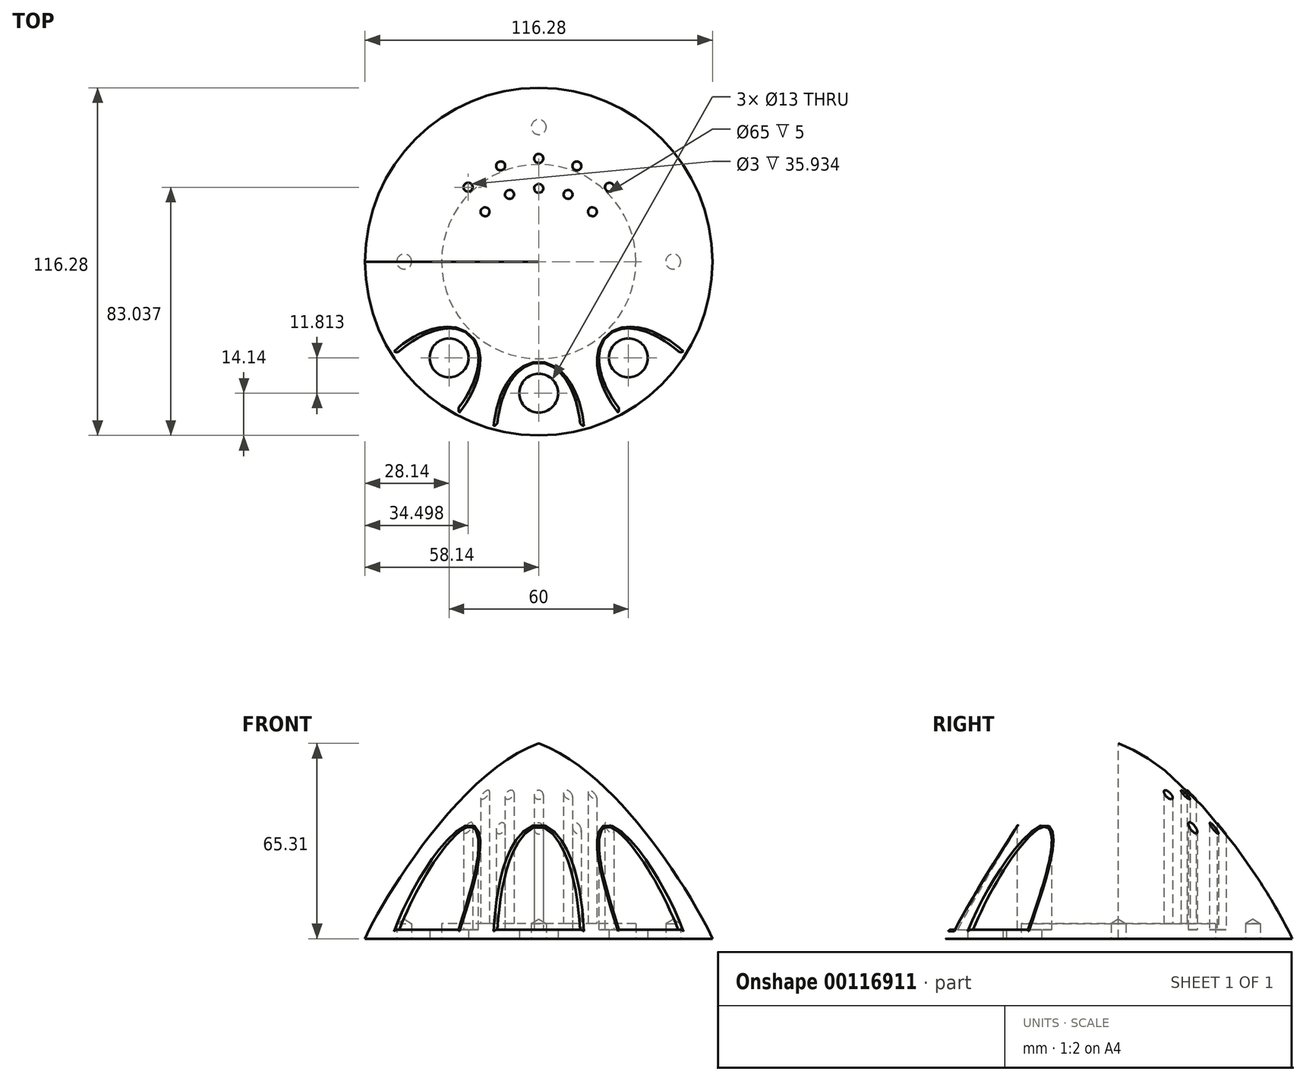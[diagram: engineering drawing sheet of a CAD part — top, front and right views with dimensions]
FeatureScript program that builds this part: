
annotation { "Feature Type Name" : "Feature", "Feature Type Description" : "" }
export const myFeature = defineFeature(function(context is Context, id is Id, definition is map)
    precondition{}
    {
        {
            var Q0;
            Q0=qCreatedBy(makeId("Top.planeOp"),FACE);
            var sketch = newSketch(context, id + "F0", { "sketchPlane" : qUnion([Q0])});
            skCircle(sketch, "E0", {"center": v(0, 0) * mm, "radius": 55 * mm});
            skCircle(sketch, "E1", {"center": v(0, 0) * mm, "radius": 32.5 * mm});
            skCircle(sketch, "E2", {"center": v(0, -44) * mm, "radius": 6.5 * mm});
            skCircle(sketch, "E3", {"center": v(-30, -32.19) * mm, "radius": 6.5 * mm});
            skCircle(sketch, "E4", {"center": v(30, -32.19) * mm, "radius": 6.5 * mm});
            skPoint(sketch, "E5", {"position": v(-45, 0) * mm});
            skPoint(sketch, "E6", {"position": v(0, 45) * mm});
            skPoint(sketch, "E7", {"position": v(45, 0) * mm});
            skSolve(sketch);
        }
        {
            var Q0;
            Q0=qCreatedBy(makeId("Top.planeOp"),FACE);
            var sketch = newSketch(context, id + "F1", { "sketchPlane" : qUnion([Q0])});
            skCircle(sketch, "E8", {"center": v(0, 0) * mm, "radius": 58.13 * mm});
            skPoint(sketch, "E9", {"position": v(-58.13, 0) * mm});
            skSolve(sketch);
        }
        {
            var Q0;
            Q0=qCreatedBy(makeId("Front.planeOp"),FACE);
            var sketch = newSketch(context, id + "F2", { "sketchPlane" : qUnion([Q0])});
            skLineSegment(sketch, "E10", {"start": v(0, 0) * mm, "end": v(-58.13, 0) * mm});
            skLineSegment(sketch, "E11", {"start": v(0, 0) * mm, "end": v(0, 65.3) * mm});
            skFitSpline(sketch, "E12", {"points": [v(-58.13, 0) * mm, v(0, 65.3) * mm], "startDerivative": vector(13.44, 31.02) * mm, "endDerivative": vector(81.7, 28.64) * mm});
            skSolve(sketch);
        }
        {
            var Q0;
            Q0=qCreatedBy(makeId("Top.planeOp"),FACE);
            cPlane(context, id + "F3", {"entities" : qUnion([Q0]), "cplaneType" : CPlaneType.OFFSET, "offset" : 3 * mm, "width" : 150 * mm, "height" : 150 * mm});
        }
        {
            var Q0;
            Q0=makeQuery(id+"F2.imprint","IMPRINT",FACE,{"disambiguationData":[TD([[makeQuery(id+"F2.imprint","IMPRINT",EDGE,{"derivedFrom":sQuery(id+"F2.wireOp",EDGE,"E10")}),-1.0]])]});
            var Q1;
            Q1=sQuery(id+"F2.wireOp",EDGE,"E11");
            revolve(context, id + "F4", {"entities" : qUnion([Q0]), "axis" : qUnion([Q1]), "revolveType" : RevolveType.FULL});
        }
        {
            var Q0;
            Q0=qCreatedBy(id+"F3.planeOp",FACE);
            var sketch = newSketch(context, id + "F5", { "sketchPlane" : qUnion([Q0])});
            skPoint(sketch, "E13", {"position": v(0, -58.13) * mm});
            skPoint(sketch, "E14", {"position": v(0, -33.5) * mm});
            skPoint(sketch, "E15", {"position": v(14, -56.42) * mm});
            skEllipse(sketch, "E16", {"center": v(0, -58.13) * mm, "majorRadius": 24.38 * mm, "minorRadius": 14.03 * mm, "majorAxis": v(0, 1)});
            skLineSegment(sketch, "E17", {"start": v(0, 0) * mm, "end": v(39.64, -42.53) * mm});
            skLineSegment(sketch, "E18", {"start": v(39.64, -42.53) * mm, "end": v(48.65, -31.82) * mm});
            skPoint(sketch, "E19", {"position": v(22.84, -24.5) * mm});
            skEllipse(sketch, "E20", {"center": v(39.64, -42.53) * mm, "majorRadius": 24.39 * mm, "minorRadius": 13.93 * mm, "majorAxis": v(-0.68, 0.73)});
            skLineSegment(sketch, "E21", {"start": v(0, 0) * mm, "end": v(-39.64, -42.53) * mm});
            skLineSegment(sketch, "E22", {"start": v(-39.64, -42.53) * mm, "end": v(-28.32, -50.77) * mm});
            skPoint(sketch, "E23", {"position": v(-22.84, -24.5) * mm});
            skEllipse(sketch, "E24", {"center": v(-39.64, -42.53) * mm, "majorRadius": 24.39 * mm, "minorRadius": 13.93 * mm, "majorAxis": v(0.68, 0.73)});
            skSolve(sketch);
        }
        {
            var Q0;
            Q0=qSketchRegion(id+"F5",true);
            extrude(context, id + "F6", {"entities" : qUnion([Q0]), "operationType" : NewBodyOperationType.REMOVE, "endBound" : BoundingType.THROUGH_ALL, "depth" : 25 * mm});
        }
        {
            var Q0;
            Q0=makeQuery(id+"F6.boolean.opBoolean","INTERSECT",EDGE,{"derivedFrom":[makeQuery(id+"F4.opRevolve","SWEPT_FACE",FACE,{"disambiguationData":[OSD([sQuery(id+"F2.wireOp",EDGE,"E12")])]}),makeQuery(id+"F6.opExtrude","SWEPT_FACE",FACE,{"disambiguationData":[OSD([sQuery(id+"F5.wireOp",EDGE,"E24")])]})]});
            var Q1;
            Q1=makeQuery(id+"F6.boolean.opBoolean","INTERSECT",EDGE,{"derivedFrom":[makeQuery(id+"F4.opRevolve","SWEPT_FACE",FACE,{"disambiguationData":[OSD([sQuery(id+"F2.wireOp",EDGE,"E12")])]}),makeQuery(id+"F6.opExtrude","CAP_FACE",FACE,{"disambiguationData":[OSD([sQuery(id+"F5.wireOp",EDGE,"E24")])],"isStart":true})]});
            var Q2;
            Q2=makeQuery(id+"F6.boolean.opBoolean","INTERSECT",EDGE,{"derivedFrom":[makeQuery(id+"F4.opRevolve","SWEPT_FACE",FACE,{"disambiguationData":[OSD([sQuery(id+"F2.wireOp",EDGE,"E12")])]}),makeQuery(id+"F6.opExtrude","SWEPT_FACE",FACE,{"disambiguationData":[OSD([sQuery(id+"F5.wireOp",EDGE,"E16")])]})]});
            var Q3;
            Q3=makeQuery(id+"F6.boolean.opBoolean","INTERSECT",EDGE,{"derivedFrom":[makeQuery(id+"F4.opRevolve","SWEPT_FACE",FACE,{"disambiguationData":[OSD([sQuery(id+"F2.wireOp",EDGE,"E12")])]}),makeQuery(id+"F6.opExtrude","CAP_FACE",FACE,{"disambiguationData":[OSD([sQuery(id+"F5.wireOp",EDGE,"E16")])],"isStart":true})]});
            var Q4;
            Q4=makeQuery(id+"F6.boolean.opBoolean","INTERSECT",EDGE,{"derivedFrom":[makeQuery(id+"F4.opRevolve","SWEPT_FACE",FACE,{"disambiguationData":[OSD([sQuery(id+"F2.wireOp",EDGE,"E12")])]}),makeQuery(id+"F6.opExtrude","SWEPT_FACE",FACE,{"disambiguationData":[OSD([sQuery(id+"F5.wireOp",EDGE,"E20")])]})]});
            var Q5;
            Q5=makeQuery(id+"F6.boolean.opBoolean","INTERSECT",EDGE,{"derivedFrom":[makeQuery(id+"F4.opRevolve","SWEPT_FACE",FACE,{"disambiguationData":[OSD([sQuery(id+"F2.wireOp",EDGE,"E12")])]}),makeQuery(id+"F6.opExtrude","CAP_FACE",FACE,{"disambiguationData":[OSD([sQuery(id+"F5.wireOp",EDGE,"E20")])],"isStart":true})]});
            fillet(context, id + "F7", {"entities" : qUnion([Q0, Q1, Q2, Q3, Q4, Q5]), "radius" : 1 * mm, "tangentPropagation" : true, "allowEdgeOverflow" : false});
        }
        {
            var Q0;
            Q0=makeQuery(id+"F0.imprint","IMPRINT",FACE,{"disambiguationData":[TD([[makeQuery(id+"F0.imprint","IMPRINT",EDGE,{"derivedFrom":sQuery(id+"F0.wireOp",EDGE,"E3")}),1.0]])]});
            var Q1;
            Q1=makeQuery(id+"F0.imprint","IMPRINT",FACE,{"disambiguationData":[TD([[makeQuery(id+"F0.imprint","IMPRINT",EDGE,{"derivedFrom":sQuery(id+"F0.wireOp",EDGE,"E2")}),1.0]])]});
            var Q2;
            Q2=makeQuery(id+"F0.imprint","IMPRINT",FACE,{"disambiguationData":[TD([[makeQuery(id+"F0.imprint","IMPRINT",EDGE,{"derivedFrom":sQuery(id+"F0.wireOp",EDGE,"E4")}),1.0]])]});
            var Q3;
            Q3=makeQuery(id+"F0.imprint","IMPRINT",FACE,{"disambiguationData":[TD([[makeQuery(id+"F0.imprint","IMPRINT",EDGE,{"derivedFrom":sQuery(id+"F0.wireOp",EDGE,"E1")}),1.0]])]});
            extrude(context, id + "F8", {"entities" : qUnion([Q0, Q1, Q2, Q3]), "operationType" : NewBodyOperationType.REMOVE, "depth" : 5 * mm});
        }
        {
            var Q0;
            Q0=sQuery(id+"F0.wireOp",VERTEX,"E5");
            var Q1;
            Q1=sQuery(id+"F0.wireOp",VERTEX,"E6");
            var Q2;
            Q2=sQuery(id+"F0.wireOp",VERTEX,"E7");
            var Q3;
            Q3=makeQuery(id+"F4.opRevolve","SWEPT_BODY",BODY,{"disambiguationData":[OSD([sQuery(id+"F2.wireOp",EDGE,"E10"),sQuery(id+"F2.wireOp",EDGE,"E11"),sQuery(id+"F2.wireOp",EDGE,"E12")])]});
            hole(context, id + "F9", {"style" : HoleStyle.SIMPLE, "holeDiameter" : 5 * mm, "endStyle" : HoleEndStyle.BLIND, "oppositeDirection" : true, "holeDepth" : 5 * mm, "locations" : qUnion([Q0, Q1, Q2]), "scope" : qUnion([Q3])});
        }
        {
            var Q0;
            Q0=qCreatedBy(id+"F3.planeOp",FACE);
            var sketch = newSketch(context, id + "F10", { "sketchPlane" : qUnion([Q0])});
            skLineSegment(sketch, "E25", {"start": v(-9.79, 22.46) * mm, "end": v(0, 24.5) * mm});
            skLineSegment(sketch, "E26", {"start": v(0, 24.5) * mm, "end": v(9.79, 22.46) * mm});
            skLineSegment(sketch, "E27", {"start": v(-9.79, 22.46) * mm, "end": v(-17.95, 16.68) * mm});
            skLineSegment(sketch, "E28", {"start": v(9.79, 22.46) * mm, "end": v(17.95, 16.68) * mm});
            skLineSegment(sketch, "E29", {"start": v(0, 34.5) * mm, "end": v(12.76, 32) * mm});
            skLineSegment(sketch, "E30", {"start": v(12.76, 32) * mm, "end": v(23.64, 24.9) * mm});
            skLineSegment(sketch, "E31", {"start": v(0, 34.5) * mm, "end": v(-12.76, 32) * mm});
            skLineSegment(sketch, "E32", {"start": v(-12.76, 32) * mm, "end": v(-23.64, 24.9) * mm});
            skSolve(sketch);
        }
        {
            var Q0;
            Q0=sQuery(id+"F10.wireOp",VERTEX,"E25.start");
            var Q1;
            Q1=sQuery(id+"F10.wireOp",VERTEX,"E26.start");
            var Q2;
            Q2=sQuery(id+"F10.wireOp",VERTEX,"E26.end");
            var Q3;
            Q3=sQuery(id+"F10.wireOp",VERTEX,"E27.end");
            var Q4;
            Q4=sQuery(id+"F10.wireOp",VERTEX,"E28.end");
            var Q5;
            Q5=sQuery(id+"F10.wireOp",VERTEX,"E32.end");
            var Q6;
            Q6=sQuery(id+"F10.wireOp",VERTEX,"E31.end");
            var Q7;
            Q7=sQuery(id+"F10.wireOp",VERTEX,"E29.start");
            var Q8;
            Q8=sQuery(id+"F10.wireOp",VERTEX,"E29.end");
            var Q9;
            Q9=sQuery(id+"F10.wireOp",VERTEX,"E30.end");
            var Q10;
            Q10=makeQuery(id+"F4.opRevolve","SWEPT_BODY",BODY,{"disambiguationData":[OSD([sQuery(id+"F2.wireOp",EDGE,"E10"),sQuery(id+"F2.wireOp",EDGE,"E11"),sQuery(id+"F2.wireOp",EDGE,"E12")])]});
            hole(context, id + "F11", {"style" : HoleStyle.SIMPLE, "holeDiameter" : 3 * mm, "endStyle" : HoleEndStyle.THROUGH, "oppositeDirection" : true, "locations" : qUnion([Q0, Q1, Q2, Q3, Q4, Q5, Q6, Q7, Q8, Q9]), "scope" : qUnion([Q10])});
        }
    });
